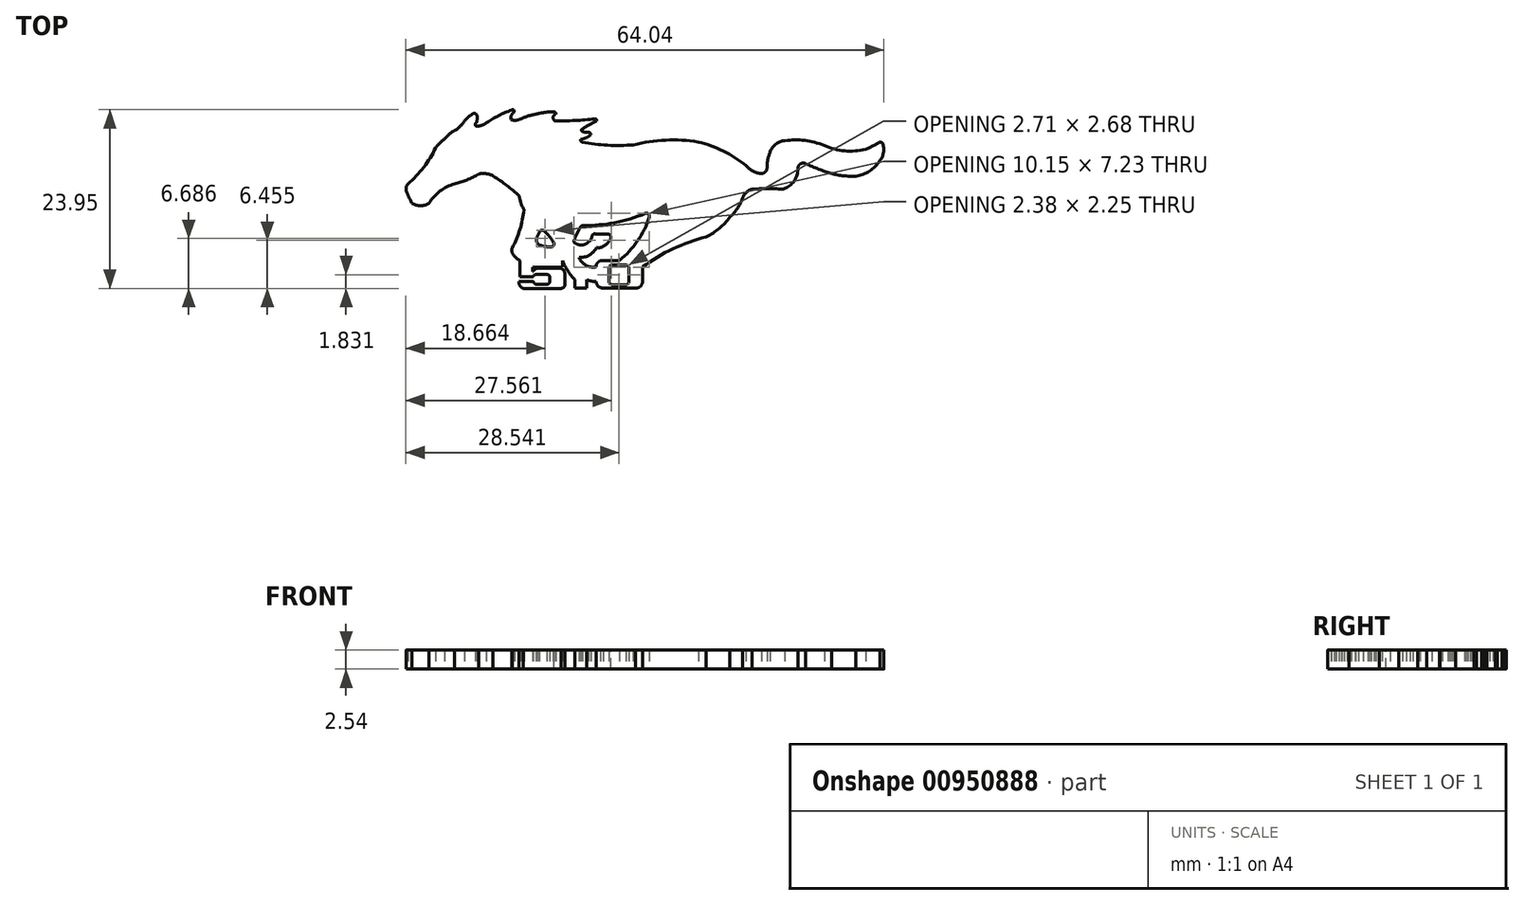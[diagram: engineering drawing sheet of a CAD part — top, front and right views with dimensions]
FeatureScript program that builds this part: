
annotation { "Feature Type Name" : "Feature", "Feature Type Description" : "" }
export const myFeature = defineFeature(function(context is Context, id is Id, definition is map)
    precondition{}
    {
        {
            var Q0;
            Q0=qCreatedBy(makeId("Top.planeOp"),FACE);
            var sketch = newSketch(context, id + "F0", { "sketchPlane" : qUnion([Q0])});
            skArc(sketch, "E0", {"start": v(-17.97, 9.65) * mm, "mid": v(-18.77, 9.1) * mm, "end": v(-19.48, 8.44) * mm});
            skArc(sketch, "E1", {"start": v(-20.85, 7.12) * mm, "mid": v(-20.08, 7.69) * mm, "end": v(-19.48, 8.44) * mm});
            skArc(sketch, "E2", {"start": v(-20.85, 7.12) * mm, "mid": v(-21.55, 6.64) * mm, "end": v(-22.13, 6) * mm});
            skArc(sketch, "E3", {"start": v(-22.13, 6) * mm, "mid": v(-22.8, 5.47) * mm, "end": v(-23.37, 4.82) * mm});
            skArc(sketch, "E4", {"start": v(-27.06, 0) * mm, "mid": v(-24.96, 2.21) * mm, "end": v(-23.37, 4.82) * mm});
            skArc(sketch, "E5", {"start": v(-27.06, 0) * mm, "mid": v(-27.3, -0.4) * mm, "end": v(-27.31, -0.88) * mm});
            skArc(sketch, "E6", {"start": v(-27.31, -0.88) * mm, "mid": v(-26.98, -1.76) * mm, "end": v(-26.52, -2.59) * mm});
            skArc(sketch, "E7", {"start": v(-26.52, -2.59) * mm, "mid": v(-25.38, -2.95) * mm, "end": v(-24.24, -2.59) * mm});
            skArc(sketch, "E8", {"start": v(-20.85, 0) * mm, "mid": v(-22.77, -1) * mm, "end": v(-24.24, -2.59) * mm});
            skArc(sketch, "E9", {"start": v(-20.85, 0) * mm, "mid": v(-19.16, 0.51) * mm, "end": v(-17.6, 1.33) * mm});
            skArc(sketch, "E10", {"start": v(-15.67, 1.06) * mm, "mid": v(-16.61, 1.37) * mm, "end": v(-17.6, 1.33) * mm});
            skArc(sketch, "E11", {"start": v(-12.13, -1.64) * mm, "mid": v(-13.84, -0.21) * mm, "end": v(-15.67, 1.06) * mm});
            skArc(sketch, "E12", {"start": v(-12.13, -1.64) * mm, "mid": v(-11.93, -2.6) * mm, "end": v(-11.5, -3.47) * mm});
            skArc(sketch, "E13", {"start": v(-13.1, -8.6) * mm, "mid": v(-12.06, -6.1) * mm, "end": v(-11.5, -3.47) * mm});
            skArc(sketch, "E14", {"start": v(-13.1, -8.6) * mm, "mid": v(-13.16, -8.93) * mm, "end": v(-13.1, -9.27) * mm});
            skArc(sketch, "E15", {"start": v(12.9, -7.11) * mm, "mid": v(14.65, -5.98) * mm, "end": v(16.08, -4.47) * mm});
            skArc(sketch, "E16", {"start": v(16.08, -4.47) * mm, "mid": v(17.08, -3.28) * mm, "end": v(17.8, -1.9) * mm});
            skArc(sketch, "E17", {"start": v(19.04, -0.72) * mm, "mid": v(18.27, -1.16) * mm, "end": v(17.8, -1.9) * mm});
            skArc(sketch, "E18", {"start": v(23.17, -0.72) * mm, "mid": v(21.1, -0.66) * mm, "end": v(19.04, -0.72) * mm});
            skArc(sketch, "E19", {"start": v(29.7, 1.36) * mm, "mid": v(31.3, 1.07) * mm, "end": v(32.93, 1.03) * mm});
            skArc(sketch, "E20", {"start": v(32.93, 1.03) * mm, "mid": v(34.8, 1.7) * mm, "end": v(36.19, 3.13) * mm});
            skArc(sketch, "E21", {"start": v(36.19, 3.13) * mm, "mid": v(36.7, 4.43) * mm, "end": v(36.4, 5.78) * mm});
            skArc(sketch, "E22", {"start": v(34.28, 4.63) * mm, "mid": v(35.38, 5.14) * mm, "end": v(36.4, 5.78) * mm});
            skArc(sketch, "E23", {"start": v(28.73, 5.13) * mm, "mid": v(31.46, 4.42) * mm, "end": v(34.28, 4.63) * mm});
            skArc(sketch, "E24", {"start": v(28.73, 5.13) * mm, "mid": v(26.13, 5.8) * mm, "end": v(23.45, 5.78) * mm});
            skArc(sketch, "E25", {"start": v(23.45, 5.78) * mm, "mid": v(22.25, 5.34) * mm, "end": v(21.49, 4.33) * mm});
            skArc(sketch, "E26", {"start": v(21.49, 4.33) * mm, "mid": v(21.17, 3.3) * mm, "end": v(21.05, 2.25) * mm});
            skArc(sketch, "E27", {"start": v(20.34, 1.37) * mm, "mid": v(20.87, 1.67) * mm, "end": v(21.05, 2.25) * mm});
            skArc(sketch, "E28", {"start": v(18.24, 2.46) * mm, "mid": v(19.18, 1.7) * mm, "end": v(20.34, 1.37) * mm});
            skArc(sketch, "E29", {"start": v(18.24, 2.46) * mm, "mid": v(15.21, 4.38) * mm, "end": v(11.84, 5.6) * mm});
            skArc(sketch, "E30", {"start": v(11.84, 5.6) * mm, "mid": v(7.46, 5.86) * mm, "end": v(3.12, 5.23) * mm});
            skArc(sketch, "E31", {"start": v(-3.74, 5.6) * mm, "mid": v(-0.32, 5.18) * mm, "end": v(3.12, 5.23) * mm});
            skArc(sketch, "E32", {"start": v(-3.96, 5.95) * mm, "mid": v(-3.91, 5.74) * mm, "end": v(-3.74, 5.6) * mm});
            skArc(sketch, "E33", {"start": v(-3.96, 5.95) * mm, "mid": v(-3.2, 6.16) * mm, "end": v(-2.57, 6.6) * mm});
            skArc(sketch, "E34", {"start": v(-2.57, 6.6) * mm, "mid": v(-2.68, 6.85) * mm, "end": v(-2.93, 6.94) * mm});
            skArc(sketch, "E35", {"start": v(-3.74, 7.02) * mm, "mid": v(-3.34, 6.92) * mm, "end": v(-2.93, 6.94) * mm});
            skArc(sketch, "E36", {"start": v(-3.66, 7.37) * mm, "mid": v(-3.8, 7.21) * mm, "end": v(-3.74, 7.02) * mm});
            skArc(sketch, "E37", {"start": v(-1.8, 8.46) * mm, "mid": v(-2.74, 7.93) * mm, "end": v(-3.66, 7.37) * mm});
            skArc(sketch, "E38", {"start": v(-1.8, 8.46) * mm, "mid": v(-1.82, 8.64) * mm, "end": v(-1.99, 8.71) * mm});
            skArc(sketch, "E39", {"start": v(-7.42, 8.46) * mm, "mid": v(-4.7, 8.49) * mm, "end": v(-1.99, 8.71) * mm});
            skArc(sketch, "E40", {"start": v(-7.57, 9.08) * mm, "mid": v(-7.6, 8.75) * mm, "end": v(-7.42, 8.46) * mm});
            skArc(sketch, "E41", {"start": v(-7.21, 9.36) * mm, "mid": v(-7.43, 9.27) * mm, "end": v(-7.57, 9.08) * mm});
            skArc(sketch, "E42", {"start": v(-7.21, 9.36) * mm, "mid": v(-7.33, 9.58) * mm, "end": v(-7.57, 9.63) * mm});
            skArc(sketch, "E43", {"start": v(-7.57, 9.63) * mm, "mid": v(-8.68, 9.58) * mm, "end": v(-9.78, 9.36) * mm});
            skArc(sketch, "E44", {"start": v(-9.78, 9.36) * mm, "mid": v(-10.9, 9.1) * mm, "end": v(-11.97, 8.71) * mm});
            skArc(sketch, "E45", {"start": v(-13.25, 8.6) * mm, "mid": v(-12.6, 8.5) * mm, "end": v(-11.97, 8.71) * mm});
            skArc(sketch, "E46", {"start": v(-12.81, 9.63) * mm, "mid": v(-13.2, 9.2) * mm, "end": v(-13.25, 8.6) * mm});
            skArc(sketch, "E47", {"start": v(-12.81, 9.63) * mm, "mid": v(-12.88, 9.88) * mm, "end": v(-13.15, 9.9) * mm});
            skArc(sketch, "E48", {"start": v(-13.15, 9.9) * mm, "mid": v(-14.91, 9.14) * mm, "end": v(-16.55, 8.15) * mm});
            skArc(sketch, "E49", {"start": v(-17.85, 7.7) * mm, "mid": v(-17.18, 7.86) * mm, "end": v(-16.55, 8.15) * mm});
            skArc(sketch, "E50", {"start": v(-17.98, 8.15) * mm, "mid": v(-18.05, 7.9) * mm, "end": v(-17.85, 7.7) * mm});
            skArc(sketch, "E51", {"start": v(-17.98, 8.15) * mm, "mid": v(-17.88, 8.24) * mm, "end": v(-17.85, 8.37) * mm});
            skArc(sketch, "E52", {"start": v(-17.85, 8.37) * mm, "mid": v(-17.8, 9.02) * mm, "end": v(-17.97, 9.65) * mm});
            skArc(sketch, "E53", {"start": v(-9.12, -6.02) * mm, "mid": v(-9.58, -6.73) * mm, "end": v(-9.86, -7.52) * mm});
            skArc(sketch, "E54", {"start": v(-9.86, -7.52) * mm, "mid": v(-9.76, -7.9) * mm, "end": v(-9.48, -8.17) * mm});
            skArc(sketch, "E55", {"start": v(-9.48, -8.17) * mm, "mid": v(-8.39, -8.45) * mm, "end": v(-7.26, -8.37) * mm});
            skArc(sketch, "E56", {"start": v(-7.26, -8.37) * mm, "mid": v(-8.08, -7.1) * mm, "end": v(-9.12, -6.02) * mm});
            skArc(sketch, "E57", {"start": v(-4.86, -7.79) * mm, "mid": v(-3.86, -8.22) * mm, "end": v(-2.87, -7.79) * mm});
            skArc(sketch, "E58", {"start": v(-2.87, -7.79) * mm, "mid": v(-2.48, -7.3) * mm, "end": v(-2.44, -6.69) * mm});
            skArc(sketch, "E59", {"start": v(-2.44, -6.69) * mm, "mid": v(-1.07, -6.75) * mm, "end": v(0.3, -6.77) * mm});
            skArc(sketch, "E60", {"start": v(-1.26, -8.55) * mm, "mid": v(-0.25, -7.86) * mm, "end": v(0.3, -6.77) * mm});
            skArc(sketch, "E61", {"start": v(-1.78, -8.55) * mm, "mid": v(-1.52, -8.56) * mm, "end": v(-1.26, -8.55) * mm});
            skArc(sketch, "E62", {"start": v(-4.13, -9.87) * mm, "mid": v(-2.76, -9.56) * mm, "end": v(-1.78, -8.55) * mm});
            skArc(sketch, "E63", {"start": v(1.25, -10.28) * mm, "mid": v(3.93, -7.32) * mm, "end": v(5.5, -3.66) * mm});
            skArc(sketch, "E64", {"start": v(-3.82, -5.6) * mm, "mid": v(0.95, -5.15) * mm, "end": v(5.5, -3.66) * mm});
            skArc(sketch, "E65", {"start": v(-3.82, -5.6) * mm, "mid": v(-4.41, -6.65) * mm, "end": v(-4.86, -7.79) * mm});
            skArc(sketch, "E66", {"start": v(26.25, 2.69) * mm, "mid": v(27.96, 1.97) * mm, "end": v(29.7, 1.36) * mm});
            skArc(sketch, "E67", {"start": v(26.25, 2.69) * mm, "mid": v(25.56, 2.69) * mm, "end": v(25.2, 2.1) * mm});
            skArc(sketch, "E68", {"start": v(23.17, -0.72) * mm, "mid": v(24.66, 0.35) * mm, "end": v(25.2, 2.1) * mm});
            skArc(sketch, "E69", {"start": v(-13.1, -9.27) * mm, "mid": v(-12.67, -9.86) * mm, "end": v(-12.08, -10.3) * mm});
            skLineSegment(sketch, "E70", {"start": v(-12.08, -10.3) * mm, "end": v(-6.37, -10.28) * mm});
            skLineSegment(sketch, "E71", {"start": v(-6.37, -11.15) * mm, "end": v(-10.34, -11.16) * mm});
            skLineSegment(sketch, "E72", {"start": v(-10.34, -11.16) * mm, "end": v(-10.33, -11.77) * mm});
            skArc(sketch, "E73", {"start": v(-9.74, -11.33) * mm, "mid": v(-10.08, -11.5) * mm, "end": v(-10.33, -11.77) * mm});
            skLineSegment(sketch, "E74", {"start": v(-9.74, -11.33) * mm, "end": v(-6.56, -11.32) * mm});
            skArc(sketch, "E75", {"start": v(-6.04, -12.1) * mm, "mid": v(-6.19, -11.64) * mm, "end": v(-6.56, -11.32) * mm});
            skLineSegment(sketch, "E76", {"start": v(-6.04, -12.1) * mm, "end": v(-6.03, -13.48) * mm});
            skArc(sketch, "E77", {"start": v(-6.56, -14.02) * mm, "mid": v(-6.19, -13.86) * mm, "end": v(-6.03, -13.48) * mm});
            skLineSegment(sketch, "E78", {"start": v(-6.56, -14.02) * mm, "end": v(-11.64, -14.02) * mm});
            skArc(sketch, "E79", {"start": v(-12.19, -13.09) * mm, "mid": v(-12.07, -13.65) * mm, "end": v(-11.64, -14.02) * mm});
            skArc(sketch, "E80", {"start": v(-10.27, -13.09) * mm, "mid": v(-10.14, -13.32) * mm, "end": v(-9.93, -13.48) * mm});
            skLineSegment(sketch, "E81", {"start": v(-9.93, -13.48) * mm, "end": v(-8.44, -13.48) * mm});
            skArc(sketch, "E82", {"start": v(-8.44, -13.48) * mm, "mid": v(-8.18, -13.36) * mm, "end": v(-8.08, -13.09) * mm});
            skLineSegment(sketch, "E83", {"start": v(-8.08, -13.09) * mm, "end": v(-8.08, -12.5) * mm});
            skArc(sketch, "E84", {"start": v(-8.08, -12.5) * mm, "mid": v(-8.2, -12.25) * mm, "end": v(-8.44, -12.17) * mm});
            skLineSegment(sketch, "E85", {"start": v(-8.44, -12.17) * mm, "end": v(-9.9, -12.17) * mm});
            skArc(sketch, "E86", {"start": v(-9.9, -12.17) * mm, "mid": v(-10.15, -12.25) * mm, "end": v(-10.3, -12.46) * mm});
            skLineSegment(sketch, "E87", {"start": v(-10.3, -12.46) * mm, "end": v(-12.08, -12.46) * mm});
            skLineSegment(sketch, "E88", {"start": v(-12.08, -12.46) * mm, "end": v(-12.08, -10.3) * mm});
            skLineSegment(sketch, "E89", {"start": v(-10.27, -13.09) * mm, "end": v(-12.19, -13.09) * mm});
            skLineSegment(sketch, "E90", {"start": v(-6.37, -10.28) * mm, "end": v(-6.37, -11.15) * mm});
            skLineSegment(sketch, "E91.bottom", {"start": v(-4.7, -12.86) * mm, "end": v(-3.1, -12.86) * mm});
            skLineSegment(sketch, "E91.top", {"start": v(-4.7, -14) * mm, "end": v(-3.1, -14) * mm});
            skLineSegment(sketch, "E91.left", {"start": v(-4.7, -12.86) * mm, "end": v(-4.7, -14) * mm});
            skLineSegment(sketch, "E91.right", {"start": v(-3.1, -12.86) * mm, "end": v(-3.1, -14) * mm});
            skArc(sketch, "E92", {"start": v(-0.91, -10.28) * mm, "mid": v(-1.58, -10.5) * mm, "end": v(-1.88, -11.15) * mm});
            skArc(sketch, "E93", {"start": v(-4.13, -9.87) * mm, "mid": v(-3.24, -10.92) * mm, "end": v(-1.88, -11.15) * mm});
            skLineSegment(sketch, "E94", {"start": v(-1.88, -11.15) * mm, "end": v(-1.88, -13.08) * mm});
            skLineSegment(sketch, "E95", {"start": v(-0.91, -14) * mm, "end": v(3.42, -14) * mm});
            skLineSegment(sketch, "E96", {"start": v(-0.91, -10.28) * mm, "end": v(3.42, -10.28) * mm});
            skArc(sketch, "E97", {"start": v(4.38, -11.15) * mm, "mid": v(4.07, -10.53) * mm, "end": v(3.42, -10.28) * mm});
            skLineSegment(sketch, "E98", {"start": v(4.38, -11.15) * mm, "end": v(4.38, -13.08) * mm});
            skArc(sketch, "E99", {"start": v(3.42, -14) * mm, "mid": v(4.1, -13.74) * mm, "end": v(4.38, -13.08) * mm});
            skLineSegment(sketch, "E100", {"start": v(1.25, -10.85) * mm, "end": v(0.37, -10.85) * mm});
            skPoint(sketch, "E100.startSnap0", {"position": v(1.25, -10.28) * mm});
            skLineSegment(sketch, "E101", {"start": v(1.25, -10.85) * mm, "end": v(2.16, -10.85) * mm});
            skArc(sketch, "E102", {"start": v(0.37, -10.85) * mm, "mid": v(-0.01, -11.01) * mm, "end": v(-0.15, -11.4) * mm});
            skLineSegment(sketch, "E103", {"start": v(-0.15, -11.4) * mm, "end": v(-0.15, -13.08) * mm});
            skLineSegment(sketch, "E104", {"start": v(0.37, -13.53) * mm, "end": v(2.16, -13.53) * mm});
            skLineSegment(sketch, "E105", {"start": v(2.55, -13.06) * mm, "end": v(2.55, -11.4) * mm});
            skArc(sketch, "E106", {"start": v(2.55, -11.4) * mm, "mid": v(2.44, -11.06) * mm, "end": v(2.16, -10.85) * mm});
            skArc(sketch, "E107", {"start": v(-1.88, -13.08) * mm, "mid": v(-1.58, -13.73) * mm, "end": v(-0.91, -14) * mm});
            skArc(sketch, "E108", {"start": v(12.9, -7.11) * mm, "mid": v(8.45, -8.72) * mm, "end": v(4.38, -11.15) * mm});
            skArc(sketch, "E109", {"start": v(-0.15, -13.08) * mm, "mid": v(0.02, -13.4) * mm, "end": v(0.37, -13.53) * mm});
            skArc(sketch, "E110", {"start": v(2.16, -13.53) * mm, "mid": v(2.44, -13.37) * mm, "end": v(2.55, -13.06) * mm});
            skArc(sketch, "E111", {"start": v(-6.37, -10.28) * mm, "mid": v(-5.66, -11.65) * mm, "end": v(-4.7, -12.86) * mm});
            skArc(sketch, "E112", {"start": v(-3.1, -12.86) * mm, "mid": v(-2.5, -13.05) * mm, "end": v(-1.88, -13.08) * mm});
            skSolve(sketch);
        }
        {
            var Q0;
            Q0 = qSketchRegion(id + "F0", true);
            extrude(context, id + "F1", {"entities" : qUnion([Q0]), "depth" : 2.54 * mm, "offsetDistance" : 25.4 * mm});
        }
        {
            var Q0;
            Q0=makeQuery(id+"F1.opExtrude","SWEPT_EDGE",EDGE,{"disambiguationData":[OSD([sQuery(id+"F0.wireOp",EDGE,"CLBQsQKG-QU9n-L8bq-N23M-JaL2zNLiRsmC"),sQuery(id+"F0.wireOp",EDGE,"TD3uE2xS-ltr0-wlYJ-LW4i-P2bbdd1SEo1G")])]});
            var Q1;
            Q1=makeQuery(id+"F1.opExtrude","SWEPT_EDGE",EDGE,{"disambiguationData":[OSD([sQuery(id+"F0.wireOp",EDGE,"QBsns0YT-pigf-kkAa-kBEe-iNnjKoNVYTv0"),sQuery(id+"F0.wireOp",EDGE,"JJBDevtD-Os15-zku3-XAn4-eNQ824AUUmrR")])]});
            var Q2;
            Q2=makeQuery(id+"F1.opExtrude","SWEPT_EDGE",EDGE,{"disambiguationData":[OSD([sQuery(id+"F0.wireOp",EDGE,"E0"),sQuery(id+"F0.wireOp",EDGE,"E52")])]});
            var Q3;
            Q3=makeQuery(id+"F1.opExtrude","SWEPT_EDGE",EDGE,{"disambiguationData":[OSD([sQuery(id+"F0.wireOp",EDGE,"E58"),sQuery(id+"F0.wireOp",EDGE,"E59")])]});
            var Q4;
            Q4=makeQuery(id+"F1.opExtrude","SWEPT_EDGE",EDGE,{"disambiguationData":[OSD([sQuery(id+"F0.wireOp",EDGE,"E59"),sQuery(id+"F0.wireOp",EDGE,"E60")])]});
            var Q5;
            Q5=makeQuery(id+"F1.opExtrude","SWEPT_EDGE",EDGE,{"disambiguationData":[OSD([sQuery(id+"F0.wireOp",EDGE,"E63"),sQuery(id+"F0.wireOp",EDGE,"E64")])]});
            var Q6;
            Q6=makeQuery(id+"F1.opExtrude","SWEPT_EDGE",EDGE,{"disambiguationData":[OSD([sQuery(id+"F0.wireOp",EDGE,"E64"),sQuery(id+"F0.wireOp",EDGE,"E65")])]});
            var Q7;
            Q7=makeQuery(id+"F1.opExtrude","SWEPT_EDGE",EDGE,{"disambiguationData":[OSD([sQuery(id+"F0.wireOp",EDGE,"E53"),sQuery(id+"F0.wireOp",EDGE,"E56")])]});
            var Q8;
            Q8=makeQuery(id+"F1.opExtrude","SWEPT_EDGE",EDGE,{"disambiguationData":[OSD([sQuery(id+"F0.wireOp",EDGE,"E55"),sQuery(id+"F0.wireOp",EDGE,"E56")])]});
            var Q9;
            Q9=makeQuery(id+"F1.opExtrude","SWEPT_EDGE",EDGE,{"disambiguationData":[OSD([sQuery(id+"F0.wireOp",EDGE,"E21"),sQuery(id+"F0.wireOp",EDGE,"E22")])]});
            var Q10;
            Q10=makeQuery(id+"F1.opExtrude","SWEPT_EDGE",EDGE,{"disambiguationData":[OSD([sQuery(id+"F0.wireOp",EDGE,"sbN2FWtu-8hbX-9UO8-Qkju-0ewBaqtbFyqO"),sQuery(id+"F0.wireOp",EDGE,"WFBrHy80-2C4L-fQm3-97Qk-fU3vxL21pzyo")])]});
            var Q11;
            Q11=makeQuery(id+"F1.opExtrude","SWEPT_EDGE",EDGE,{"disambiguationData":[OSD([sQuery(id+"F0.wireOp",EDGE,"wcsMRR56-WqbC-39vy-6M11-gQQ4SU8Q0AeT"),sQuery(id+"F0.wireOp",EDGE,"CLBQsQKG-QU9n-L8bq-N23M-JaL2zNLiRsmC")])]});
            var Q12;
            Q12=makeQuery(id+"F1.opExtrude","SWEPT_EDGE",EDGE,{"disambiguationData":[OSD([sQuery(id+"F0.wireOp",EDGE,"JJBDevtD-Os15-zku3-XAn4-eNQ824AUUmrR"),sQuery(id+"F0.wireOp",EDGE,"btyeAN04-iLEZ-LbVc-waQ7-vkTmfaM2PC8D")])]});
            var Q13;
            Q13=makeQuery(id+"F1.opExtrude","SWEPT_EDGE",EDGE,{"disambiguationData":[OSD([sQuery(id+"F0.wireOp",EDGE,"E18"),sQuery(id+"F0.wireOp",EDGE,"E68")])]});
            fillet(context, id + "F2", {"entities" : qUnion([Q0, Q1, Q2, Q3, Q4, Q5, Q6, Q7, Q8, Q9, Q10, Q11, Q12, Q13]), "radius" : 0.38 * mm, "tangentPropagation" : true, "allowEdgeOverflow" : false});
        }
    });
